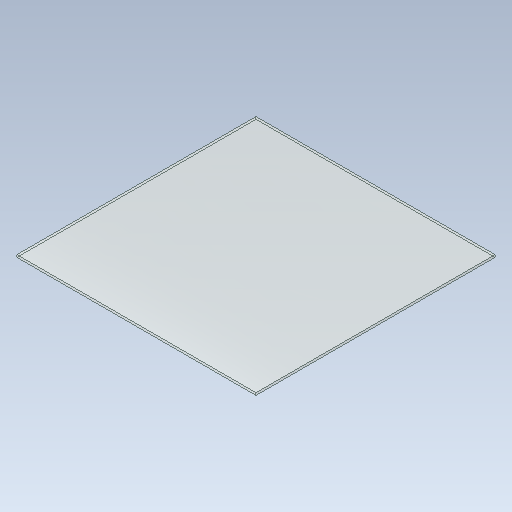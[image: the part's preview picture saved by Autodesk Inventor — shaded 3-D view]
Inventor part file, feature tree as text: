
AUTODESK INVENTOR PART (.ipt)
format: ipt  version: 2020 (Build 240168000, 168)  size: 95,232 bytes
history: native  units: mm
features: other x1, extrude x1, sketch x1
ambient origin geometry x8: Origin, YZ Plane, XZ Plane, XY Plane, X Axis, Y Axis, Z Axis, Center Point
bodies: Body1 (feature_tree)
feature tree (3):
  other  "Bryła1"
  extrude  "Wyciągnięcie proste1"  Depth=50.0mm
  sketch  "Szkic1"
